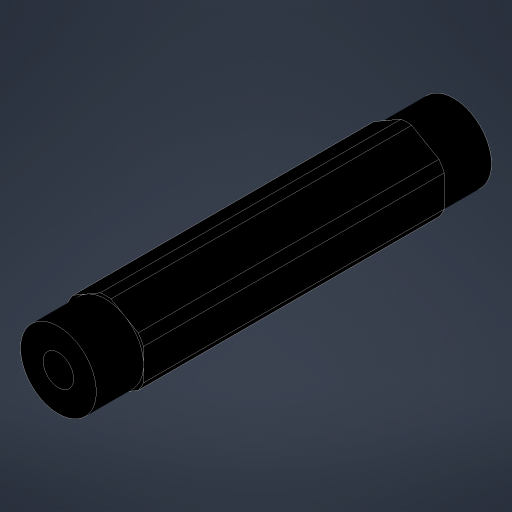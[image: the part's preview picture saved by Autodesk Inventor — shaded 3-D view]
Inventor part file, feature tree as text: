
AUTODESK INVENTOR PART (.ipt)
format: ipt  version: 2023.4 (Build 274418000, 418)  size: 237,056 bytes
history: native  units: in
note: dims shown in document units (in); Inventor stores cm internally (conversion verified against a paired STEP export)
features: extrude x3, projected_geometry x3, hole x1, mirror x1, sketch x1
ambient origin geometry x8: Origin, YZ Plane, XZ Plane, XY Plane, X Axis, Y Axis, Z Axis, Center Point
bodies: Solid1 (feature_tree)
feature tree (9):
  extrude  "Extrusion1"  Depth=0.5in
  hole  "Hole1"  [1 undecoded]
  extrude  "Extrusion3"  Depth=0.312in TaperAngle=0.0deg
  extrude  "Extrusion4"  Depth=0.5in
  mirror  "Mirror2"
  sketch  "Sketch5"  dims[d2=0.0in d9=0.625in d10=0.385in d11=0.25in d12=0.5635in d13=1.0in d14=0.8108in d16=0.7in d17=0.0in d18=0.0in d19=0.312in d20=0.0in d21=0.5in]
  projected_geometry  "Projected Loop2"
  projected_geometry  "Project Cut Edges1"
  projected_geometry  "Project Cut Edges2"
note: 1 required parameter value undecoded (feature->parameter linkage not recoverable at this tier; creation-order binding heuristic only, values carry confidence <= 0.55)
